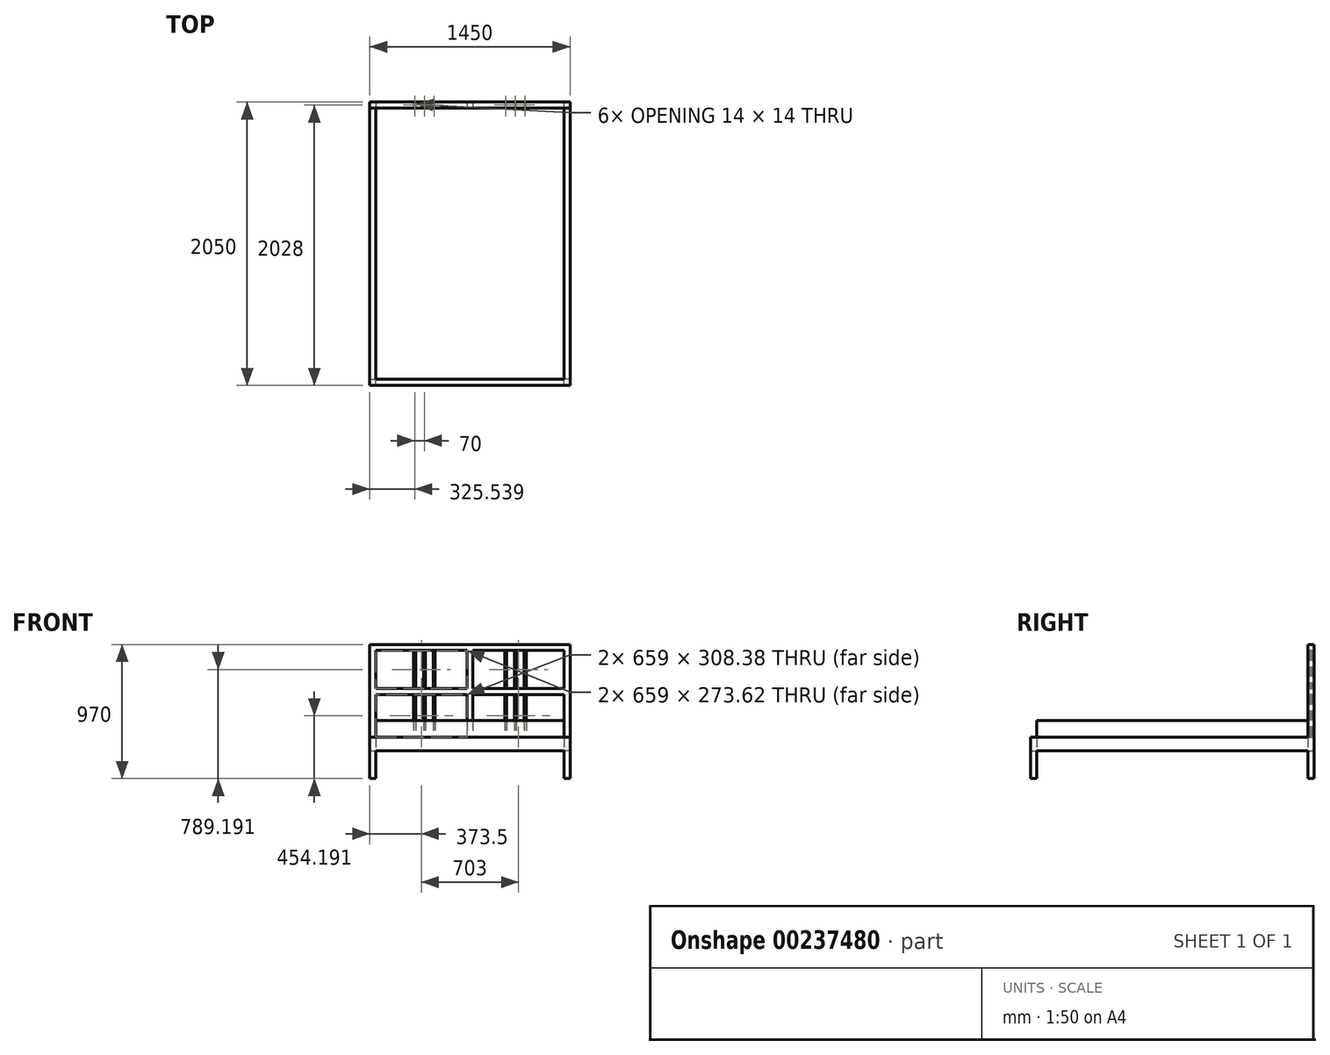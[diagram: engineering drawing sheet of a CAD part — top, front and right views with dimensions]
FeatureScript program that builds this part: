
annotation { "Feature Type Name" : "Feature", "Feature Type Description" : "" }
export const myFeature = defineFeature(function(context is Context, id is Id, definition is map)
    precondition{}
    {
        {
            var Q0;
            Q0=qCreatedBy(makeId("Top.planeOp"),FACE);
            var sketch = newSketch(context, id + "F0", { "sketchPlane" : qUnion([Q0])});
            skLineSegment(sketch, "E0.bottom", {"start": v(0, 0) * mm, "end": v(1450, 0) * mm});
            skLineSegment(sketch, "E0.top", {"start": v(0, -2050) * mm, "end": v(1450, -2050) * mm});
            skLineSegment(sketch, "E0.left", {"start": v(0, 0) * mm, "end": v(0, -2050) * mm});
            skLineSegment(sketch, "E0.right", {"start": v(1450, 0) * mm, "end": v(1450, -2050) * mm});
            skLineSegment(sketch, "E1.0", {"start": v(1406, -44) * mm, "end": v(1406, -2006) * mm});
            skLineSegment(sketch, "E1.1", {"start": v(44, -44) * mm, "end": v(1406, -44) * mm});
            skLineSegment(sketch, "E1.2", {"start": v(44, -44) * mm, "end": v(44, -2006) * mm});
            skLineSegment(sketch, "E1.3", {"start": v(44, -2006) * mm, "end": v(1406, -2006) * mm});
            skSolve(sketch);
        }
        {
            var Q0;
            Q0=makeQuery(id+"F0.imprint","IMPRINT",FACE,{"disambiguationData":[TD([[makeQuery(id+"F0.imprint","IMPRINT",EDGE,{"derivedFrom":sQuery(id+"F0.wireOp",EDGE,"E0.bottom")}),-1.0]])]});
            extrude(context, id + "F1", {"entities" : qUnion([Q0]), "depth" : 100 * mm});
        }
        {
            var Q0;
            Q0=makeQuery(id+"F1.opExtrude","CAP_FACE",FACE,{"disambiguationData":[OSD([sQuery(id+"F0.wireOp",EDGE,"E0.bottom"),sQuery(id+"F0.wireOp",EDGE,"E0.top"),sQuery(id+"F0.wireOp",EDGE,"E0.left"),sQuery(id+"F0.wireOp",EDGE,"E0.right"),sQuery(id+"F0.wireOp",EDGE,"E1.0"),sQuery(id+"F0.wireOp",EDGE,"E1.1"),sQuery(id+"F0.wireOp",EDGE,"E1.2"),sQuery(id+"F0.wireOp",EDGE,"E1.3")])],"isStart":false});
            var sketch = newSketch(context, id + "F2", { "sketchPlane" : qUnion([Q0])});
            skLineSegment(sketch, "E2.bottom", {"start": v(1406, -44) * mm, "end": v(1450, -44) * mm});
            skLineSegment(sketch, "E2.top", {"start": v(1406, 0) * mm, "end": v(1450, 0) * mm});
            skLineSegment(sketch, "E2.left", {"start": v(1406, -44) * mm, "end": v(1406, 0) * mm});
            skLineSegment(sketch, "E2.right", {"start": v(1450, -44) * mm, "end": v(1450, 0) * mm});
            skLineSegment(sketch, "E3.bottom", {"start": v(44, -44) * mm, "end": v(0, -44) * mm});
            skLineSegment(sketch, "E3.top", {"start": v(44, 0) * mm, "end": v(0, 0) * mm});
            skLineSegment(sketch, "E3.left", {"start": v(44, -44) * mm, "end": v(44, 0) * mm});
            skLineSegment(sketch, "E3.right", {"start": v(0, -44) * mm, "end": v(0, 0) * mm});
            skLineSegment(sketch, "E4.bottom", {"start": v(747, -44) * mm, "end": v(703, -44) * mm});
            skLineSegment(sketch, "E4.top", {"start": v(747, 0) * mm, "end": v(703, 0) * mm});
            skLineSegment(sketch, "E4.left", {"start": v(747, -44) * mm, "end": v(747, 0) * mm});
            skLineSegment(sketch, "E4.right", {"start": v(703, -44) * mm, "end": v(703, 0) * mm});
            skLineSegment(sketch, "E5", {"start": v(725, 0) * mm, "end": v(725, -44) * mm, "construction": true});
            skCircle(sketch, "E6", {"center": v(1054.46, -22) * mm, "radius": 7 * mm});
            skCircle(sketch, "E7", {"center": v(984.46, -22) * mm, "radius": 7 * mm});
            skCircle(sketch, "E8", {"center": v(1124.46, -22) * mm, "radius": 7 * mm});
            skLineSegment(sketch, "E9", {"start": v(984.46, -22) * mm, "end": v(1124.46, -22) * mm, "construction": true});
            skCircle(sketch, "E10.MirrorC", {"center": v(465.54, -22) * mm, "radius": 7 * mm});
            skCircle(sketch, "E11.MirrorC", {"center": v(395.54, -22) * mm, "radius": 7 * mm});
            skCircle(sketch, "E12.MirrorC", {"center": v(325.54, -22) * mm, "radius": 7 * mm});
            skSolve(sketch);
        }
        {
            var Q0;
            Q0=qSketchRegion(id+"F2",true);
            extrude(context, id + "F3", {"entities" : qUnion([Q0]), "operationType" : NewBodyOperationType.ADD, "depth" : 670 * mm});
        }
        {
            var Q0;
            Q0=makeQuery(id+"F3.opExtrude","SWEPT_FACE",FACE,{"disambiguationData":[OSD([sQuery(id+"F2.wireOp",EDGE,"E3.left")])]});
            var sketch = newSketch(context, id + "F4", { "sketchPlane" : qUnion([Q0])});
            skLineSegment(sketch, "E13.bottom", {"start": v(-44, 770) * mm, "end": v(0, 770) * mm});
            skLineSegment(sketch, "E13.top", {"start": v(-44, 726) * mm, "end": v(0, 726) * mm});
            skLineSegment(sketch, "E13.left", {"start": v(-44, 770) * mm, "end": v(-44, 726) * mm});
            skLineSegment(sketch, "E13.right", {"start": v(0, 770) * mm, "end": v(0, 726) * mm});
            skLineSegment(sketch, "E14.bottom", {"start": v(0, 452.38) * mm, "end": v(-44, 452.38) * mm});
            skLineSegment(sketch, "E14.top", {"start": v(0, 408.38) * mm, "end": v(-44, 408.38) * mm});
            skLineSegment(sketch, "E14.left", {"start": v(0, 452.38) * mm, "end": v(0, 408.38) * mm});
            skLineSegment(sketch, "E14.right", {"start": v(-44, 452.38) * mm, "end": v(-44, 408.38) * mm});
            skSolve(sketch);
        }
        {
            var Q0;
            Q0=qSketchRegion(id+"F4",true);
            var Q1;
            Q1=makeQuery(id+"F3.opExtrude","SWEPT_FACE",FACE,{"disambiguationData":[OSD([sQuery(id+"F2.wireOp",EDGE,"E2.left")])]});
            extrude(context, id + "F5", {"entities" : qUnion([Q0]), "operationType" : NewBodyOperationType.ADD, "endBound" : BoundingType.UP_TO_SURFACE, "endBoundEntityFace" : qUnion([Q1]), "depth" : 25 * mm});
        }
        {
            var Q0;
            Q0=makeQuery(id+"F0.imprint","IMPRINT",FACE,{"disambiguationData":[TD([[makeQuery(id+"F0.imprint","IMPRINT",EDGE,{"derivedFrom":sQuery(id+"F0.wireOp",EDGE,"E0.bottom")}),-1.0]])]});
            var sketch = newSketch(context, id + "F6", { "sketchPlane" : qUnion([Q0])});
            skLineSegment(sketch, "E15.bottom", {"start": v(0, 0) * mm, "end": v(44, 0) * mm});
            skLineSegment(sketch, "E15.top", {"start": v(0, -44) * mm, "end": v(44, -44) * mm});
            skLineSegment(sketch, "E15.left", {"start": v(0, 0) * mm, "end": v(0, -44) * mm});
            skLineSegment(sketch, "E15.right", {"start": v(44, 0) * mm, "end": v(44, -44) * mm});
            skLineSegment(sketch, "E16.bottom", {"start": v(1406, -44) * mm, "end": v(1450, -44) * mm});
            skLineSegment(sketch, "E16.top", {"start": v(1406, 0) * mm, "end": v(1450, 0) * mm});
            skLineSegment(sketch, "E16.left", {"start": v(1406, -44) * mm, "end": v(1406, 0) * mm});
            skLineSegment(sketch, "E16.right", {"start": v(1450, -44) * mm, "end": v(1450, 0) * mm});
            skLineSegment(sketch, "E17.bottom", {"start": v(1450, -2050) * mm, "end": v(1406, -2050) * mm});
            skLineSegment(sketch, "E17.top", {"start": v(1450, -2006) * mm, "end": v(1406, -2006) * mm});
            skLineSegment(sketch, "E17.left", {"start": v(1450, -2050) * mm, "end": v(1450, -2006) * mm});
            skLineSegment(sketch, "E17.right", {"start": v(1406, -2050) * mm, "end": v(1406, -2006) * mm});
            skLineSegment(sketch, "E18.bottom", {"start": v(0, -2050) * mm, "end": v(44, -2050) * mm});
            skLineSegment(sketch, "E18.top", {"start": v(0, -2006) * mm, "end": v(44, -2006) * mm});
            skLineSegment(sketch, "E18.left", {"start": v(0, -2050) * mm, "end": v(0, -2006) * mm});
            skLineSegment(sketch, "E18.right", {"start": v(44, -2050) * mm, "end": v(44, -2006) * mm});
            skSolve(sketch);
        }
        {
            var Q0;
            Q0=qSketchRegion(id+"F6",true);
            extrude(context, id + "F7", {"entities" : qUnion([Q0]), "operationType" : NewBodyOperationType.ADD, "oppositeDirection" : true, "depth" : 200 * mm});
        }
        {
            var Q0;
            Q0=makeQuery(id+"F0.imprint","IMPRINT",FACE,{"disambiguationData":[TD([[makeQuery(id+"F0.imprint","IMPRINT",EDGE,{"derivedFrom":sQuery(id+"F0.wireOp",EDGE,"E1.0")}),-1.0]])]});
            extrude(context, id + "F8", {"entities" : qUnion([Q0]), "depth" : 220 * mm});
        }
    });
